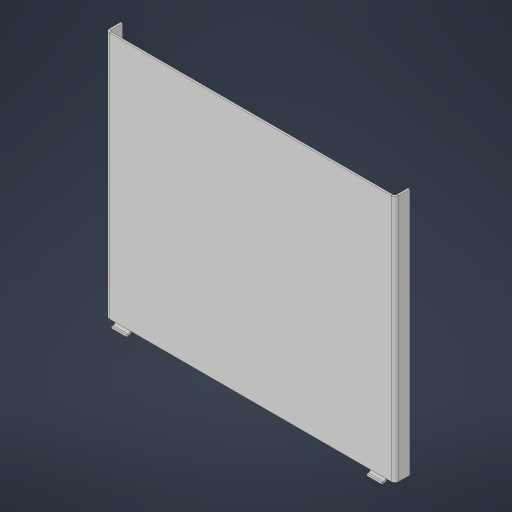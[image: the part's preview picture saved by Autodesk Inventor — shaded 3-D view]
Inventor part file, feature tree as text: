
AUTODESK INVENTOR PART (.ipt)
format: ipt  version: 2023.4 (Build 274418000, 418)  size: 223,232 bytes
history: native  units: in
note: dims shown in document units (in); Inventor stores cm internally (conversion verified against a paired STEP export)
features: sheet_metal_op x7, sketch x3, other x3, projected_geometry x1
ambient origin geometry x8: Origin, YZ Plane, XZ Plane, XY Plane, X Axis, Y Axis, Z Axis, Center Point
bodies: Solid1 (feature_tree)
feature tree (14):
  sheet_metal_op  "Face1"
  sheet_metal_op  "Flange1"
  sketch  "Sketch3"  dims[d2=0.12in d3=0.12in d4=0.06in d5=0.24in d6=0.12in d7=1.0in d8=90.0deg d9=0.12in d10=0.48in d11=0.12in d12=0.12in d13=0.375in d14=1.0in d15=8.0in d16=8.0in d17=1.0in d18=0.12in d19=0.12in d20=0.06in d21=0.24in d22=0.12in d23=0.25in d24=0.12in d25=0.06in d26=0.24in d27=0.12in d28=90.0deg d29=0.12in]
  sheet_metal_op  "Face2"
  sheet_metal_op  "Fold1"
  sketch  "Sketch1"  dims[d0=19.25in]
  other  "Plate1"
  sketch  "Sketch2"  dims[d1=16.5in]
  other  "Plate2"
  sheet_metal_op  "Bend1"
  sheet_metal_op  "Corner1"
  other  "Plate3"
  sheet_metal_op  "Bend2"
  projected_geometry  "Project Cut Edges1"
